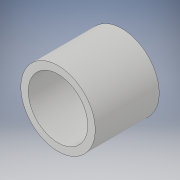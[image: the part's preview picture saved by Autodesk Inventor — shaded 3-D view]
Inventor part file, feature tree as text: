
AUTODESK INVENTOR PART (.ipt)
format: ipt  version: 2019 (Build 230136000, 136)  size: 101,888 bytes
history: native  units: mm
features: extrude x2, sketch x2
ambient origin geometry x8: Origin, YZ Plane, XZ Plane, XY Plane, X Axis, Y Axis, Z Axis, Center Point
bodies: Solid1 (feature_tree)
feature tree (4):
  extrude  "Extrusion1"  Depth=215.0mm TaperAngle=0.0deg
  extrude  "Extrusion2"  Depth=21.5mm TaperAngle=0.0deg
  sketch  "Sketch1"  dims[d0=250.0mm d1=215.0mm d2=0.0mm]
  sketch  "Sketch2"  dims[d3=200.0mm d4=21.5mm d5=0.0mm]
